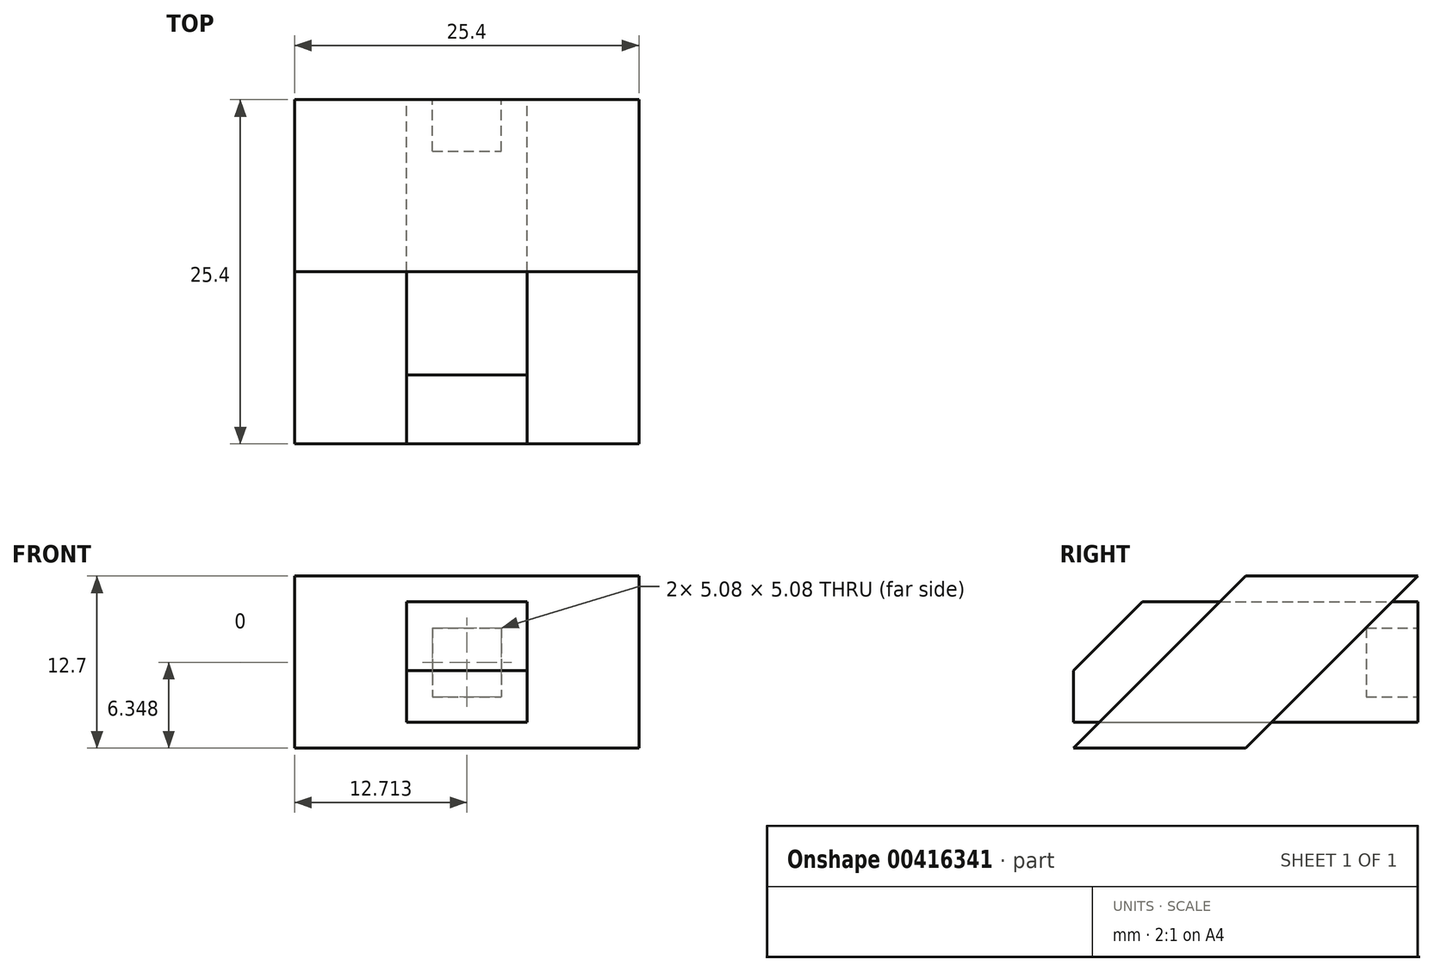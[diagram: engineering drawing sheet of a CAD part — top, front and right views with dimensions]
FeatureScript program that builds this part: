
annotation { "Feature Type Name" : "Feature", "Feature Type Description" : "" }
export const myFeature = defineFeature(function(context is Context, id is Id, definition is map)
    precondition{}
    {
        {
            var Q0;
            Q0=qCreatedBy(makeId("Front.planeOp"),FACE);
            var sketch = newSketch(context, id + "F0", { "sketchPlane" : qUnion([Q0])});
            skLineSegment(sketch, "E0", {"start": v(0, 12.7) * mm, "end": v(-25.4, 12.7) * mm});
            skLineSegment(sketch, "E1", {"start": v(-25.4, 12.7) * mm, "end": v(-25.4, 0) * mm});
            skLineSegment(sketch, "E2", {"start": v(-25.4, 0) * mm, "end": v(0, 0) * mm});
            skLineSegment(sketch, "E3", {"start": v(0, 0) * mm, "end": v(0, 12.7) * mm});
            skSolve(sketch);
        }
        {
            var Q0;
            Q0 = qSketchRegion(id + "F0", true);
            extrude(context, id + "F1", {"entities" : qUnion([Q0]), "depth" : 25.4 * mm});
        }
        {
            var Q0;
            Q0=makeQuery(id+"F1.opExtrude","CAP_EDGE",EDGE,{"disambiguationData":[OSD([sQuery(id+"F0.wireOp",EDGE,"E0")])],"isStart":false});
            var Q1;
            Q1=makeQuery(id+"F1.opExtrude","CAP_EDGE",EDGE,{"disambiguationData":[OSD([sQuery(id+"F0.wireOp",EDGE,"E2")])],"isStart":true});
            chamfer(context, id + "F2", {"entities" : qUnion([Q0, Q1]), "width" : 12.7 * mm, "tangentPropagation" : true});
        }
        {
            var Q0;
            Q0=qCreatedBy(makeId("Front.planeOp"),FACE);
            var sketch = newSketch(context, id + "F3", { "sketchPlane" : qUnion([Q0])});
            skLineSegment(sketch, "E4.bottom", {"start": v(-17.14, 10.8) * mm, "end": v(-8.25, 10.8) * mm});
            skLineSegment(sketch, "E4.top", {"start": v(-17.14, 1.9) * mm, "end": v(-8.25, 1.9) * mm});
            skLineSegment(sketch, "E4.left", {"start": v(-17.14, 10.8) * mm, "end": v(-17.14, 1.9) * mm});
            skLineSegment(sketch, "E4.right", {"start": v(-8.25, 10.8) * mm, "end": v(-8.25, 1.9) * mm});
            skPoint(sketch, "E4.middle", {"position": v(-12.7, 6.35) * mm});
            skSolve(sketch);
        }
        {
            var Q0;
            Q0 = qSketchRegion(id + "F3", true);
            extrude(context, id + "F4", {"entities" : qUnion([Q0]), "depth" : 25.4 * mm});
        }
        {
            var Q0;
            Q0=makeQuery(id+"F3.imprint","IMPRINT",FACE,{"disambiguationData":[TD([[makeQuery(id+"F3.imprint","IMPRINT",EDGE,{"derivedFrom":sQuery(id+"F3.wireOp",EDGE,"E4.bottom")}),-1.0]])]});
            var sketch = newSketch(context, id + "F5", { "sketchPlane" : qUnion([Q0])});
            skPoint(sketch, "E5.middle", {"position": v(-12.69, 6.35) * mm});
            skLineSegment(sketch, "E6.bottom", {"start": v(-15.23, 8.89) * mm, "end": v(-10.15, 8.89) * mm});
            skLineSegment(sketch, "E6.top", {"start": v(-15.23, 3.8) * mm, "end": v(-10.15, 3.8) * mm});
            skLineSegment(sketch, "E6.left", {"start": v(-15.23, 8.89) * mm, "end": v(-15.23, 3.8) * mm});
            skLineSegment(sketch, "E6.right", {"start": v(-10.15, 8.89) * mm, "end": v(-10.15, 3.8) * mm});
            skSolve(sketch);
        }
        {
            var Q0;
            Q0 = qSketchRegion(id + "F5", true);
            extrude(context, id + "F6", {"entities" : qUnion([Q0]), "operationType" : NewBodyOperationType.REMOVE, "oppositeDirection" : true, "depth" : -3.8 * mm});
        }
        {
            var Q0;
            Q0=makeQuery(id+"F4.opExtrude","CAP_EDGE",EDGE,{"disambiguationData":[OSD([sQuery(id+"F3.wireOp",EDGE,"E4.bottom")])],"isStart":false});
            chamfer(context, id + "F7", {"entities" : qUnion([Q0]), "width" : 5.08 * mm, "tangentPropagation" : true});
        }
    });
